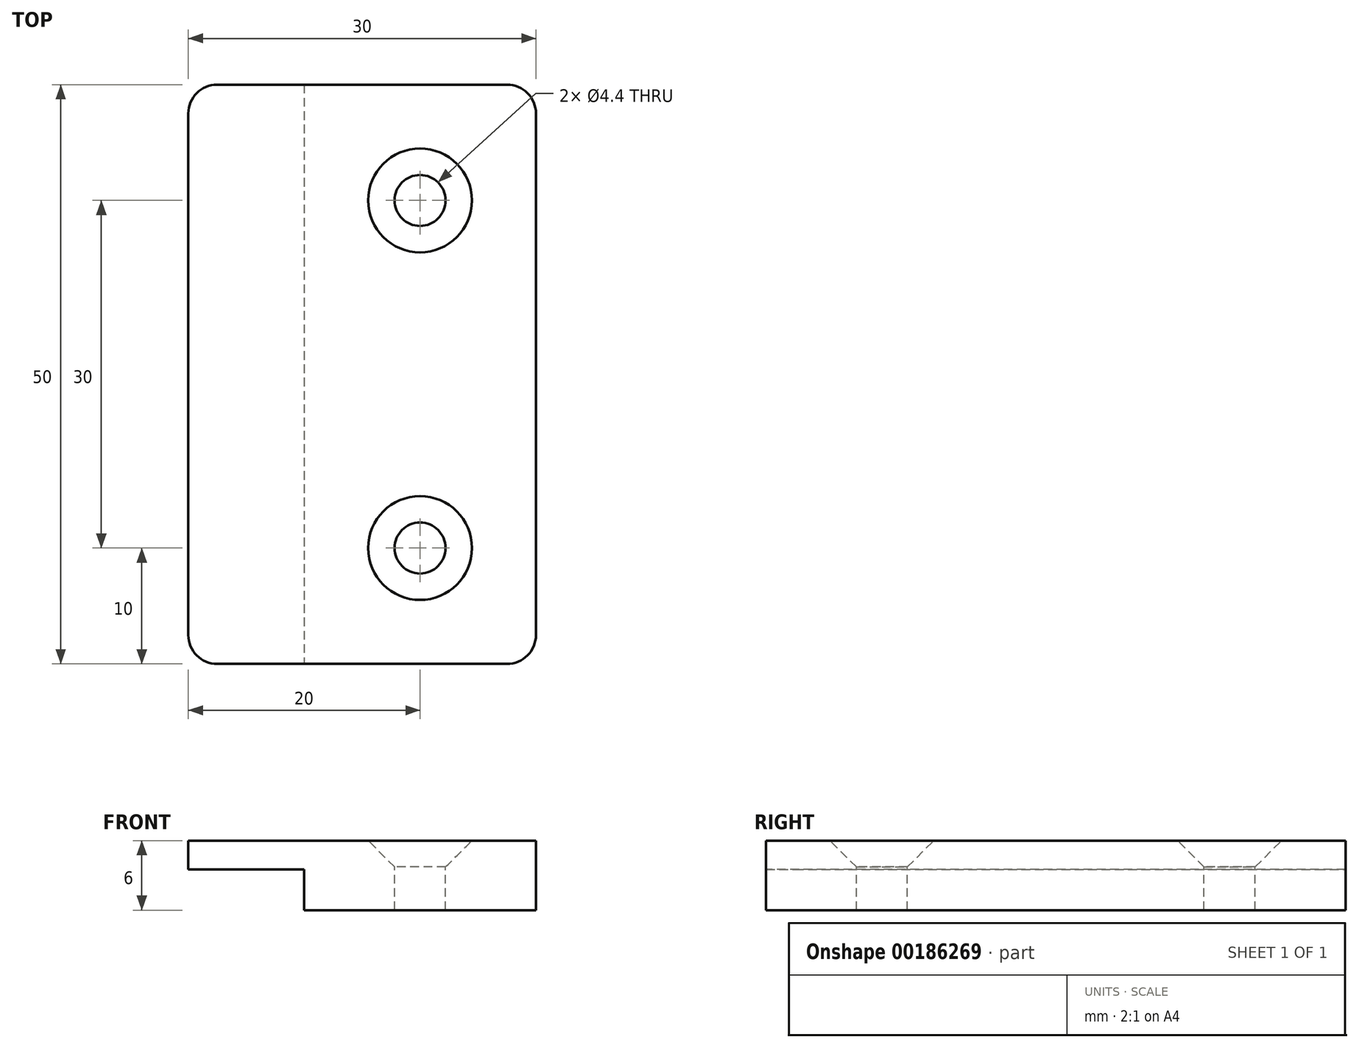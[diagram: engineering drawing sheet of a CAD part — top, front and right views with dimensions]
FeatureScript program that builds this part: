
annotation { "Feature Type Name" : "Feature", "Feature Type Description" : "" }
export const myFeature = defineFeature(function(context is Context, id is Id, definition is map)
    precondition{}
    {
        {
            var Q0;
            Q0=qCreatedBy(makeId("Top.planeOp"),FACE);
            var sketch = newSketch(context, id + "F0", { "sketchPlane" : qUnion([Q0])});
            skLineSegment(sketch, "E0.bottom", {"start": v(15, -25) * mm, "end": v(-15, -25) * mm});
            skLineSegment(sketch, "E0.top", {"start": v(15, 25) * mm, "end": v(-15, 25) * mm});
            skLineSegment(sketch, "E0.left", {"start": v(15, -25) * mm, "end": v(15, 25) * mm});
            skLineSegment(sketch, "E0.right", {"start": v(-15, -25) * mm, "end": v(-15, 25) * mm});
            skPoint(sketch, "E0.middle", {"position": v(0, 0) * mm});
            skSolve(sketch);
        }
        {
            var Q0;
            Q0=makeQuery(id+"F0.imprint","IMPRINT",FACE,{"disambiguationData":[TD([[makeQuery(id+"F0.imprint","IMPRINT",EDGE,{"derivedFrom":sQuery(id+"F0.wireOp",EDGE,"E0.bottom")}),-1.0]])]});
            extrude(context, id + "F1", {"entities" : qUnion([Q0]), "depth" : 6 * mm, "offsetDistance" : 25 * mm});
        }
        {
            var Q0;
            Q0=makeQuery(id+"F1.opExtrude","CAP_FACE",FACE,{"disambiguationData":[OSD([sQuery(id+"F0.wireOp",EDGE,"E0.bottom"),sQuery(id+"F0.wireOp",EDGE,"E0.top"),sQuery(id+"F0.wireOp",EDGE,"E0.left"),sQuery(id+"F0.wireOp",EDGE,"E0.right")])],"isStart":false});
            var sketch = newSketch(context, id + "F2", { "sketchPlane" : qUnion([Q0])});
            skPoint(sketch, "E1", {"position": v(5, 15) * mm});
            skPoint(sketch, "E2", {"position": v(5, -15) * mm});
            skSolve(sketch);
        }
        {
            var Q0;
            Q0=sQuery(id+"F2.wireOp",VERTEX,"E1");
            var Q1;
            Q1=sQuery(id+"F2.wireOp",VERTEX,"E2");
            var Q2;
            Q2=makeQuery(id+"F1.opExtrude","SWEPT_BODY",BODY,{"disambiguationData":[OSD([sQuery(id+"F0.wireOp",EDGE,"E0.bottom"),sQuery(id+"F0.wireOp",EDGE,"E0.top"),sQuery(id+"F0.wireOp",EDGE,"E0.left"),sQuery(id+"F0.wireOp",EDGE,"E0.right")])]});
            hole(context, id + "F3", {"style" : HoleStyle.C_SINK, "endStyle" : HoleEndStyle.THROUGH, "standardTappedOrClearance" : lookupTablePath({ "standard" : "ISO", "fit" : "Normal", "size" : "M4", "type" : "Clearance" }), "standardBlindInLast" : lookupTablePath({ "fit" : "Standard", "standard" : "ISO", "size" : "M4", "type" : "Clearance" }), "holeDiameter" : 4.4 * mm, "cSinkDiameter" : 8.96 * mm, "cSinkAngle" : 90 * degree, "majorDiameter" : 5 * mm, "isTappedThrough" : true, "tappedDepth" : 12 * mm, "tapClearance" : 3, "startFromSketch" : true, "locations" : qUnion([Q0, Q1]), "scope" : qUnion([Q2])});
        }
        {
            var Q0;
            Q0=makeQuery(id+"F1.opExtrude","CAP_FACE",FACE,{"disambiguationData":[OSD([sQuery(id+"F0.wireOp",EDGE,"E0.bottom"),sQuery(id+"F0.wireOp",EDGE,"E0.top"),sQuery(id+"F0.wireOp",EDGE,"E0.left"),sQuery(id+"F0.wireOp",EDGE,"E0.right")])],"isStart":true});
            var sketch = newSketch(context, id + "F4", { "sketchPlane" : qUnion([Q0])});
            skPoint(sketch, "E3", {"position": v(-5, -25) * mm});
            skPoint(sketch, "E4", {"position": v(-5, 25) * mm});
            skLineSegment(sketch, "E5", {"start": v(-5, -25) * mm, "end": v(-5, 25) * mm});
            skSolve(sketch);
        }
        {
            var Q0;
            {var subQ0=sQuery(id+"F4.wireOp",EDGE,"E5");Q0=makeQuery(id+"F4.imprint","IMPRINT",FACE,{"disambiguationData":[TD([[makeQuery(id+"F4.imprint","IMPRINT",EDGE,{"derivedFrom":subQ0}),1.0]])]});}
            extrude(context, id + "F5", {"entities" : qUnion([Q0]), "operationType" : NewBodyOperationType.REMOVE, "oppositeDirection" : true, "depth" : 3.5 * mm, "offsetDistance" : 25 * mm});
        }
        {
            var Q0;
            Q0=makeQuery(id+"F1.opExtrude","SWEPT_EDGE",EDGE,{"disambiguationData":[OSD([sQuery(id+"F0.wireOp",EDGE,"E0.bottom"),sQuery(id+"F0.wireOp",EDGE,"E0.right")])]});
            var Q1;
            Q1=makeQuery(id+"F1.opExtrude","SWEPT_EDGE",EDGE,{"disambiguationData":[OSD([sQuery(id+"F0.wireOp",EDGE,"E0.bottom"),sQuery(id+"F0.wireOp",EDGE,"E0.left")])]});
            var Q2;
            Q2=makeQuery(id+"F1.opExtrude","SWEPT_EDGE",EDGE,{"disambiguationData":[OSD([sQuery(id+"F0.wireOp",EDGE,"E0.top"),sQuery(id+"F0.wireOp",EDGE,"E0.right")])]});
            var Q3;
            Q3=makeQuery(id+"F1.opExtrude","SWEPT_EDGE",EDGE,{"disambiguationData":[OSD([sQuery(id+"F0.wireOp",EDGE,"E0.top"),sQuery(id+"F0.wireOp",EDGE,"E0.left")])]});
            fillet(context, id + "F6", {"entities" : qUnion([Q0, Q1, Q2, Q3]), "radius" : 2.5 * mm, "tangentPropagation" : true, "allowEdgeOverflow" : false});
        }
    });
